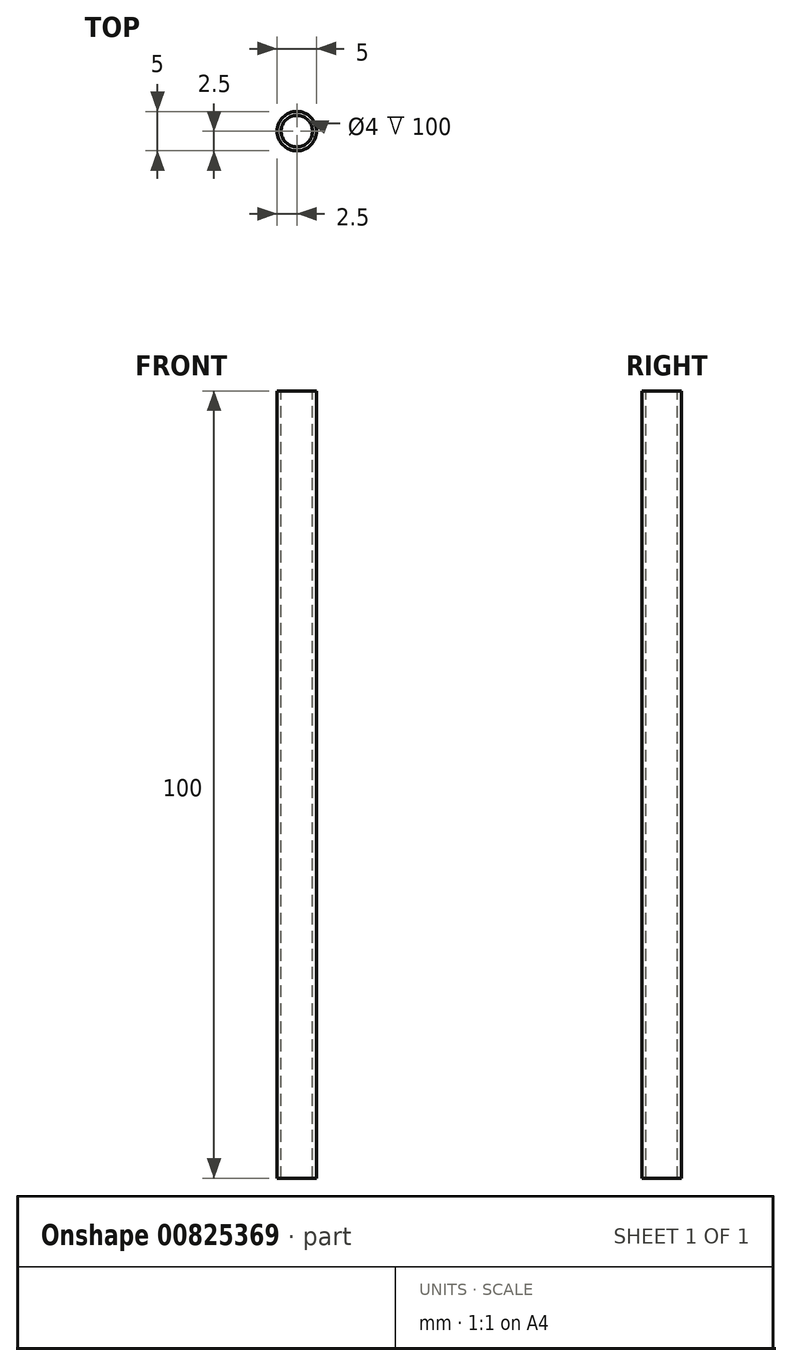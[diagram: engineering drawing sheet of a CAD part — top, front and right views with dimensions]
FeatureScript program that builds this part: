
annotation { "Feature Type Name" : "Feature", "Feature Type Description" : "" }
export const myFeature = defineFeature(function(context is Context, id is Id, definition is map)
    precondition{}
    {
        {
            var Q0;
            Q0=qCreatedBy(makeId("Top.planeOp"),FACE);
            var sketch = newSketch(context, id + "F0", { "sketchPlane" : qUnion([Q0])});
            skCircle(sketch, "E0", {"center": v(0, 0) * mm, "radius": 2.5 * mm});
            skSolve(sketch);
        }
        {
            var Q0;
            Q0 = qSketchRegion(id + "F0", true);
            extrude(context, id + "F1", {"entities" : qUnion([Q0]), "oppositeDirection" : true, "depth" : 100 * mm, "offsetDistance" : 25 * mm});
        }
        {
            var Q0;
            Q0=makeQuery(id+"F1.opExtrude","CAP_FACE",FACE,{"disambiguationData":[OSD([sQuery(id+"F0.wireOp",EDGE,"E0")])],"isStart":true});
            var sketch = newSketch(context, id + "F2", { "sketchPlane" : qUnion([Q0])});
            skCircle(sketch, "E1", {"center": v(0, 0) * mm, "radius": 2 * mm});
            skSolve(sketch);
        }
        {
            var Q0;
            Q0 = qSketchRegion(id + "F2", true);
            extrude(context, id + "F3", {"entities" : qUnion([Q0]), "operationType" : NewBodyOperationType.REMOVE, "oppositeDirection" : true, "depth" : 101 * mm, "offsetDistance" : 25 * mm});
        }
    });
